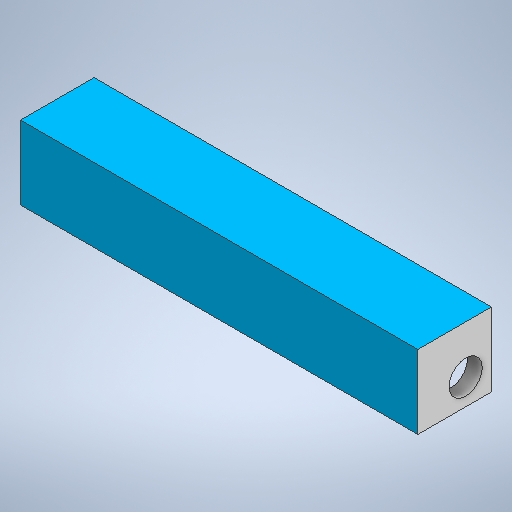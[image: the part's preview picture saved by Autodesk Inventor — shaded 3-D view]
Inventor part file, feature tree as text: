
AUTODESK INVENTOR PART (.ipt)
format: ipt  version: 2025.1 (Build 291241020, 241B)  size: 253,440 bytes
history: native  units: mm
features: sketch x4, extrude x4, hole x1
ambient origin geometry x8: Origin, YZ Plane, XZ Plane, XY Plane, X Axis, Y Axis, Z Axis, Center Point
bodies: Solid1 (feature_tree)
feature tree (9):
  sketch  "Sketch1"  dims[d0=54.0mm d1=10.0mm]
  extrude  "Extrusion1"  Depth=10.0mm
  extrude  "Extrusion2"  Depth=2.0mm TaperAngle=0.0deg
  extrude  "Extrusion3"  Depth=10.0mm
  extrude  "Extrusion4"  Depth=2.0mm TaperAngle=0.0deg
  hole  "Hole1"  [1 undecoded]
  sketch  "Sketch2"  dims[d3=2.0mm d4=2.0mm d5=0.0mm]
  sketch  "Sketch3"  dims[d6=10.0mm d7=0.0mm d8=10.0mm]
  sketch  "Sketch5"  dims[d9=10.0mm d10=2.0mm d11=0.0mm d12=2.0mm d13=0.0mm d19=3.5mm d20=3.5mm d21=4.5mm d22=6.0mm d23=9.4mm d24=2.0mm d25=90.0deg d26=8.0mm d27=20.594885mm]
note: 1 required parameter value undecoded (feature->parameter linkage not recoverable at this tier; creation-order binding heuristic only, values carry confidence <= 0.55)
